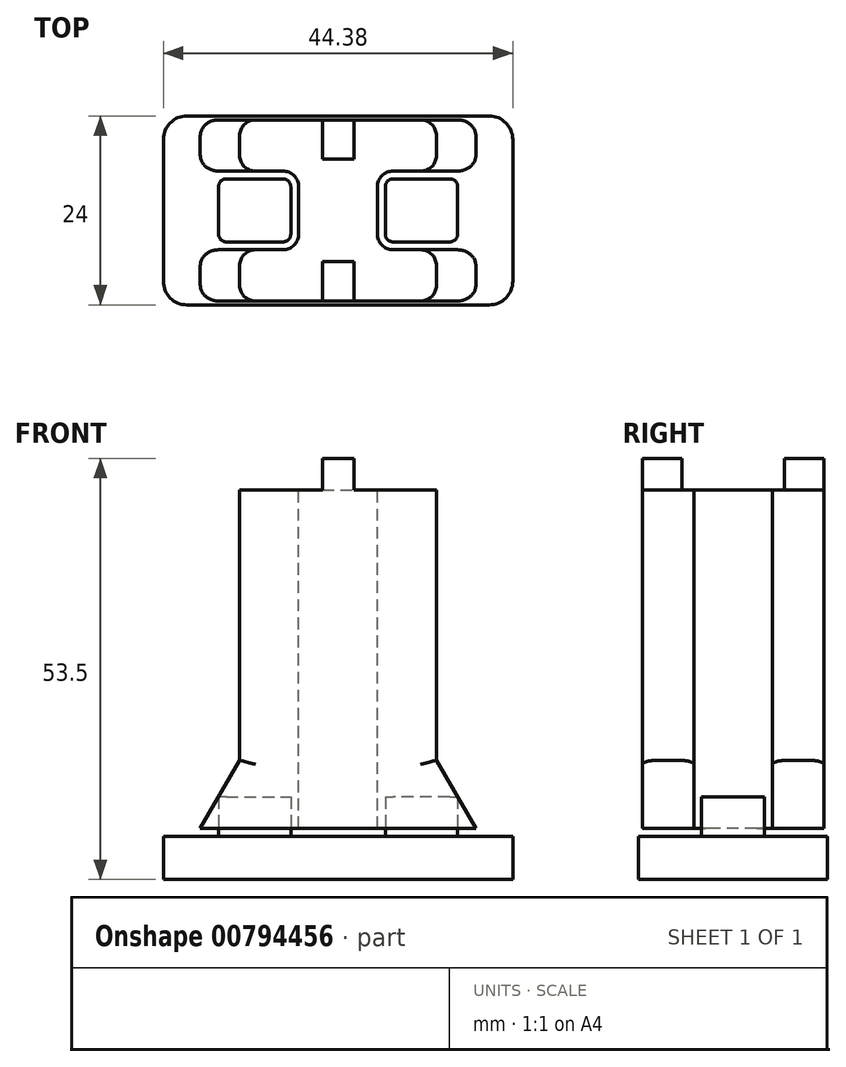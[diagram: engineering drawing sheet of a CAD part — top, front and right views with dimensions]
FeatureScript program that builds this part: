
annotation { "Feature Type Name" : "Feature", "Feature Type Description" : "" }
export const myFeature = defineFeature(function(context is Context, id is Id, definition is map)
    precondition{}
    {
        {
            var Q0;
            Q0=qCreatedBy(makeId("Top.planeOp"),FACE);
            var sketch = newSketch(context, id + "F0", { "sketchPlane" : qUnion([Q0])});
            skLineSegment(sketch, "E0.bottom", {"start": v(0, 0) * mm, "end": v(25, 0) * mm});
            skLineSegment(sketch, "E0.top", {"start": v(0, -23) * mm, "end": v(25, -23) * mm});
            skLineSegment(sketch, "E0.left", {"start": v(0, 0) * mm, "end": v(0, -23) * mm});
            skLineSegment(sketch, "E0.right", {"start": v(25, 0) * mm, "end": v(25, -23) * mm});
            skSolve(sketch);
        }
        {
            var Q0;
            Q0 = qSketchRegion(id + "F0", true);
            extrude(context, id + "F1", {"entities" : qUnion([Q0]), "depth" : 43 * mm, "offsetDistance" : 25 * mm});
        }
        {
            var Q0;
            Q0=makeQuery(id+"F1.opExtrude","CAP_FACE",FACE,{"disambiguationData":[OSD([sQuery(id+"F0.wireOp",EDGE,"E0.bottom"),sQuery(id+"F0.wireOp",EDGE,"E0.top"),sQuery(id+"F0.wireOp",EDGE,"E0.left"),sQuery(id+"F0.wireOp",EDGE,"E0.right")])],"isStart":false});
            var sketch = newSketch(context, id + "F2", { "sketchPlane" : qUnion([Q0])});
            skLineSegment(sketch, "E1.bottom", {"start": v(10.5, 0) * mm, "end": v(14.5, 0) * mm});
            skLineSegment(sketch, "E1.top", {"start": v(10.5, -5) * mm, "end": v(14.5, -5) * mm});
            skLineSegment(sketch, "E1.left", {"start": v(10.5, 0) * mm, "end": v(10.5, -5) * mm});
            skLineSegment(sketch, "E1.right", {"start": v(14.5, 0) * mm, "end": v(14.5, -5) * mm});
            skLineSegment(sketch, "E2.bottom", {"start": v(10.5, -23) * mm, "end": v(14.5, -23) * mm});
            skLineSegment(sketch, "E2.top", {"start": v(10.5, -18) * mm, "end": v(14.5, -18) * mm});
            skLineSegment(sketch, "E2.left", {"start": v(10.5, -23) * mm, "end": v(10.5, -18) * mm});
            skLineSegment(sketch, "E2.right", {"start": v(14.5, -23) * mm, "end": v(14.5, -18) * mm});
            skSolve(sketch);
        }
        {
            var Q0;
            Q0 = qSketchRegion(id + "F2", true);
            extrude(context, id + "F3", {"entities" : qUnion([Q0]), "operationType" : NewBodyOperationType.ADD, "depth" : 4 * mm, "offsetDistance" : 25 * mm});
        }
        {
            var Q0;
            Q0=makeQuery(id+"F3.boolean.opBoolean","MERGE",FACE,{"derivedFrom":[makeQuery(id+"F1.opExtrude","SWEPT_FACE",FACE,{"disambiguationData":[OSD([sQuery(id+"F0.wireOp",EDGE,"E0.top")])]}),makeQuery(id+"F3.opExtrude","SWEPT_FACE",FACE,{"disambiguationData":[OSD([sQuery(id+"F2.wireOp",EDGE,"E2.bottom")])]})]});
            var sketch = newSketch(context, id + "F4", { "sketchPlane" : qUnion([Q0])});
            skLineSegment(sketch, "E3", {"start": v(25, 8.66) * mm, "end": v(30, 0) * mm});
            skLineSegment(sketch, "E4", {"start": v(30, 0) * mm, "end": v(25, 0) * mm});
            skLineSegment(sketch, "E5", {"start": v(25, 0) * mm, "end": v(25, 8.66) * mm});
            skLineSegment(sketch, "E6", {"start": v(0, 8.66) * mm, "end": v(-5, 0) * mm});
            skLineSegment(sketch, "E7", {"start": v(-5, 0) * mm, "end": v(0, 0) * mm});
            skLineSegment(sketch, "E8", {"start": v(0, 0) * mm, "end": v(0, 8.66) * mm});
            skSolve(sketch);
        }
        {
            var Q0;
            Q0 = qSketchRegion(id + "F4", true);
            extrude(context, id + "F5", {"entities" : qUnion([Q0]), "operationType" : NewBodyOperationType.ADD, "oppositeDirection" : true, "depth" : 23 * mm, "offsetDistance" : 25 * mm});
        }
        {
            var Q0;
            Q0=makeQuery(id+"F1.opExtrude","CAP_FACE",FACE,{"disambiguationData":[OSD([sQuery(id+"F0.wireOp",EDGE,"E0.bottom"),sQuery(id+"F0.wireOp",EDGE,"E0.top"),sQuery(id+"F0.wireOp",EDGE,"E0.left"),sQuery(id+"F0.wireOp",EDGE,"E0.right")])],"isStart":false});
            var sketch = newSketch(context, id + "F6", { "sketchPlane" : qUnion([Q0])});
            skLineSegment(sketch, "E9.bottom", {"start": v(-7.5, -6.5) * mm, "end": v(7.5, -6.5) * mm});
            skLineSegment(sketch, "E9.top", {"start": v(-7.5, -16.5) * mm, "end": v(7.5, -16.5) * mm});
            skLineSegment(sketch, "E9.left", {"start": v(-7.5, -6.5) * mm, "end": v(-7.5, -16.5) * mm});
            skLineSegment(sketch, "E9.right", {"start": v(7.5, -6.5) * mm, "end": v(7.5, -16.5) * mm});
            skPoint(sketch, "E9.middle", {"position": v(0, -11.5) * mm});
            skLineSegment(sketch, "E10.bottom", {"start": v(32.5, -6.5) * mm, "end": v(17.5, -6.5) * mm});
            skLineSegment(sketch, "E10.top", {"start": v(32.5, -16.5) * mm, "end": v(17.5, -16.5) * mm});
            skLineSegment(sketch, "E10.left", {"start": v(32.5, -6.5) * mm, "end": v(32.5, -16.5) * mm});
            skLineSegment(sketch, "E10.right", {"start": v(17.5, -6.5) * mm, "end": v(17.5, -16.5) * mm});
            skPoint(sketch, "E10.middle", {"position": v(25, -11.5) * mm});
            skPoint(sketch, "E10.cornerSnap0", {"position": v(0, -6.5) * mm});
            skSolve(sketch);
        }
        {
            var Q0;
            Q0 = qSketchRegion(id + "F6", true);
            extrude(context, id + "F7", {"entities" : qUnion([Q0]), "operationType" : NewBodyOperationType.REMOVE, "endBound" : BoundingType.THROUGH_ALL, "oppositeDirection" : true, "depth" : 25 * mm, "offsetDistance" : 25 * mm});
        }
        {
            var Q0;
            Q0=makeQuery(id+"F1.opExtrude","SWEPT_EDGE",EDGE,{"disambiguationData":[OSD([sQuery(id+"F0.wireOp",EDGE,"E0.top"),sQuery(id+"F0.wireOp",EDGE,"E0.right")])]});
            var Q1;
            Q1=makeQuery(id+"F5.opExtrude","CAP_EDGE",EDGE,{"disambiguationData":[OSD([sQuery(id+"F4.wireOp",EDGE,"E3")])],"isStart":true});
            var Q2;
            Q2=makeQuery(id+"F1.opExtrude","SWEPT_EDGE",EDGE,{"disambiguationData":[OSD([sQuery(id+"F0.wireOp",EDGE,"E0.top"),sQuery(id+"F0.wireOp",EDGE,"E0.left")])]});
            var Q3;
            Q3=makeQuery(id+"F7.boolean.opBoolean","INTERSECT",EDGE,{"derivedFrom":[makeQuery(id+"F1.opExtrude","SWEPT_FACE",FACE,{"disambiguationData":[OSD([sQuery(id+"F0.wireOp",EDGE,"E0.left")])]}),makeQuery(id+"F7.opExtrude","SWEPT_FACE",FACE,{"disambiguationData":[OSD([sQuery(id+"F6.wireOp",EDGE,"E9.top")])]})]});
            var Q4;
            Q4=makeQuery(id+"F5.opExtrude","CAP_EDGE",EDGE,{"disambiguationData":[OSD([sQuery(id+"F4.wireOp",EDGE,"E6")])],"isStart":true});
            var Q5;
            Q5=makeQuery(id+"F7.boolean.opBoolean","INTERSECT",EDGE,{"derivedFrom":[makeQuery(id+"F5.opExtrude","SWEPT_FACE",FACE,{"disambiguationData":[OSD([sQuery(id+"F4.wireOp",EDGE,"E6")])]}),makeQuery(id+"F7.opExtrude","SWEPT_FACE",FACE,{"disambiguationData":[OSD([sQuery(id+"F6.wireOp",EDGE,"E9.top")])]})]});
            var Q6;
            Q6=makeQuery(id+"F7.boolean.opBoolean","COPY",EDGE,{"derivedFrom":makeQuery(id+"F7.opExtrude","SWEPT_EDGE",EDGE,{"disambiguationData":[OSD([sQuery(id+"F6.wireOp",EDGE,"E9.top"),sQuery(id+"F6.wireOp",EDGE,"E9.right")])]})});
            var Q7;
            Q7=makeQuery(id+"F7.boolean.opBoolean","COPY",EDGE,{"derivedFrom":makeQuery(id+"F7.opExtrude","SWEPT_EDGE",EDGE,{"disambiguationData":[OSD([sQuery(id+"F6.wireOp",EDGE,"E9.bottom"),sQuery(id+"F6.wireOp",EDGE,"E9.right")])]})});
            var Q8;
            Q8=makeQuery(id+"F7.boolean.opBoolean","INTERSECT",EDGE,{"derivedFrom":[makeQuery(id+"F1.opExtrude","SWEPT_FACE",FACE,{"disambiguationData":[OSD([sQuery(id+"F0.wireOp",EDGE,"E0.left")])]}),makeQuery(id+"F7.opExtrude","SWEPT_FACE",FACE,{"disambiguationData":[OSD([sQuery(id+"F6.wireOp",EDGE,"E9.bottom")])]})]});
            var Q9;
            Q9=makeQuery(id+"F7.boolean.opBoolean","INTERSECT",EDGE,{"derivedFrom":[makeQuery(id+"F5.opExtrude","SWEPT_FACE",FACE,{"disambiguationData":[OSD([sQuery(id+"F4.wireOp",EDGE,"E6")])]}),makeQuery(id+"F7.opExtrude","SWEPT_FACE",FACE,{"disambiguationData":[OSD([sQuery(id+"F6.wireOp",EDGE,"E9.bottom")])]})]});
            var Q10;
            Q10=makeQuery(id+"F1.opExtrude","SWEPT_EDGE",EDGE,{"disambiguationData":[OSD([sQuery(id+"F0.wireOp",EDGE,"E0.bottom"),sQuery(id+"F0.wireOp",EDGE,"E0.left")])]});
            var Q11;
            Q11=makeQuery(id+"F5.opExtrude","CAP_EDGE",EDGE,{"disambiguationData":[OSD([sQuery(id+"F4.wireOp",EDGE,"E6")])],"isStart":false});
            var Q12;
            Q12=makeQuery(id+"F7.boolean.opBoolean","COPY",EDGE,{"derivedFrom":makeQuery(id+"F7.opExtrude","SWEPT_EDGE",EDGE,{"disambiguationData":[OSD([sQuery(id+"F6.wireOp",EDGE,"E10.top"),sQuery(id+"F6.wireOp",EDGE,"E10.right")])]})});
            var Q13;
            Q13=makeQuery(id+"F7.boolean.opBoolean","INTERSECT",EDGE,{"derivedFrom":[makeQuery(id+"F1.opExtrude","SWEPT_FACE",FACE,{"disambiguationData":[OSD([sQuery(id+"F0.wireOp",EDGE,"E0.right")])]}),makeQuery(id+"F7.opExtrude","SWEPT_FACE",FACE,{"disambiguationData":[OSD([sQuery(id+"F6.wireOp",EDGE,"E10.top")])]})]});
            var Q14;
            Q14=makeQuery(id+"F7.boolean.opBoolean","INTERSECT",EDGE,{"derivedFrom":[makeQuery(id+"F5.opExtrude","SWEPT_FACE",FACE,{"disambiguationData":[OSD([sQuery(id+"F4.wireOp",EDGE,"E3")])]}),makeQuery(id+"F7.opExtrude","SWEPT_FACE",FACE,{"disambiguationData":[OSD([sQuery(id+"F6.wireOp",EDGE,"E10.top")])]})]});
            var Q15;
            Q15=makeQuery(id+"F5.opExtrude","CAP_EDGE",EDGE,{"disambiguationData":[OSD([sQuery(id+"F4.wireOp",EDGE,"E3")])],"isStart":false});
            var Q16;
            Q16=makeQuery(id+"F1.opExtrude","SWEPT_EDGE",EDGE,{"disambiguationData":[OSD([sQuery(id+"F0.wireOp",EDGE,"E0.bottom"),sQuery(id+"F0.wireOp",EDGE,"E0.right")])]});
            var Q17;
            Q17=makeQuery(id+"F7.boolean.opBoolean","COPY",EDGE,{"derivedFrom":makeQuery(id+"F7.opExtrude","SWEPT_EDGE",EDGE,{"disambiguationData":[OSD([sQuery(id+"F6.wireOp",EDGE,"E10.bottom"),sQuery(id+"F6.wireOp",EDGE,"E10.right")])]})});
            var Q18;
            Q18=makeQuery(id+"F7.boolean.opBoolean","INTERSECT",EDGE,{"derivedFrom":[makeQuery(id+"F1.opExtrude","SWEPT_FACE",FACE,{"disambiguationData":[OSD([sQuery(id+"F0.wireOp",EDGE,"E0.right")])]}),makeQuery(id+"F7.opExtrude","SWEPT_FACE",FACE,{"disambiguationData":[OSD([sQuery(id+"F6.wireOp",EDGE,"E10.bottom")])]})]});
            var Q19;
            Q19=makeQuery(id+"F7.boolean.opBoolean","INTERSECT",EDGE,{"derivedFrom":[makeQuery(id+"F5.opExtrude","SWEPT_FACE",FACE,{"disambiguationData":[OSD([sQuery(id+"F4.wireOp",EDGE,"E3")])]}),makeQuery(id+"F7.opExtrude","SWEPT_FACE",FACE,{"disambiguationData":[OSD([sQuery(id+"F6.wireOp",EDGE,"E10.bottom")])]})]});
            fillet(context, id + "F8", {"entities" : qUnion([Q0, Q1, Q2, Q3, Q4, Q5, Q6, Q7, Q8, Q9, Q10, Q11, Q12, Q13, Q14, Q15, Q16, Q17, Q18, Q19]), "radius" : 2 * mm, "tangentPropagation" : true, "allowEdgeOverflow" : false});
        }
        {
            var Q0;
            Q0=makeQuery(id+"F5.boolean.opBoolean","MERGE",FACE,{"derivedFrom":[makeQuery(id+"F1.opExtrude","CAP_FACE",FACE,{"disambiguationData":[OSD([sQuery(id+"F0.wireOp",EDGE,"E0.bottom"),sQuery(id+"F0.wireOp",EDGE,"E0.top"),sQuery(id+"F0.wireOp",EDGE,"E0.left"),sQuery(id+"F0.wireOp",EDGE,"E0.right")])],"isStart":true}),makeQuery(id+"F5.opExtrude","SWEPT_FACE",FACE,{"disambiguationData":[OSD([sQuery(id+"F4.wireOp",EDGE,"E4")])]}),makeQuery(id+"F5.opExtrude","SWEPT_FACE",FACE,{"disambiguationData":[OSD([sQuery(id+"F4.wireOp",EDGE,"E7")])]})]});
            var sketch = newSketch(context, id + "F9", { "sketchPlane" : qUnion([Q0])});
            skLineSegment(sketch, "E11.0", {"start": v(-2.7, 15.5) * mm, "end": v(5.5, 15.5) * mm});
            skLineSegment(sketch, "E12.0", {"start": v(6.5, 8.5) * mm, "end": v(6.5, 14.5) * mm});
            skLineSegment(sketch, "E13.0", {"start": v(-2.7, 7.5) * mm, "end": v(5.5, 7.5) * mm});
            skLineSegment(sketch, "E14.0", {"start": v(18.5, 8.5) * mm, "end": v(18.5, 14.5) * mm});
            skLineSegment(sketch, "E15.0", {"start": v(27.7, 15.5) * mm, "end": v(19.5, 15.5) * mm});
            skLineSegment(sketch, "E16.0", {"start": v(27.7, 7.5) * mm, "end": v(19.5, 7.5) * mm});
            skArc(sketch, "E17", {"start": v(6.5, 14.5) * mm, "mid": v(6.2, 15.2) * mm, "end": v(5.5, 15.5) * mm});
            skArc(sketch, "E18", {"start": v(5.5, 7.5) * mm, "mid": v(6.2, 7.8) * mm, "end": v(6.5, 8.5) * mm});
            skArc(sketch, "E19", {"start": v(19.5, 15.5) * mm, "mid": v(18.8, 15.2) * mm, "end": v(18.5, 14.5) * mm});
            skArc(sketch, "E20", {"start": v(18.5, 8.5) * mm, "mid": v(18.8, 7.8) * mm, "end": v(19.5, 7.5) * mm});
            skLineSegment(sketch, "E21", {"start": v(27.7, 15.5) * mm, "end": v(27.7, 7.5) * mm});
            skLineSegment(sketch, "E22", {"start": v(-2.7, 15.5) * mm, "end": v(-2.7, 7.5) * mm});
            skSolve(sketch);
        }
        {
            var Q0;
            Q0 = qSketchRegion(id + "F9", true);
            extrude(context, id + "F10", {"entities" : qUnion([Q0]), "oppositeDirection" : true, "depth" : 4 * mm, "offsetDistance" : 25 * mm, "hasSecondDirection" : true, "secondDirectionOppositeDirection" : false, "secondDirectionDepth" : 1 * mm});
        }
        {
            var Q0;
            Q0=makeQuery(id+"F10.opExtrude","CAP_FACE",FACE,{"disambiguationData":[OSD([sQuery(id+"F9.wireOp",EDGE,"E11.0"),sQuery(id+"F9.wireOp",EDGE,"E12.0"),sQuery(id+"F9.wireOp",EDGE,"E13.0"),sQuery(id+"F9.wireOp",EDGE,"E17"),sQuery(id+"F9.wireOp",EDGE,"E18"),sQuery(id+"F9.wireOp",EDGE,"E22")])],"isStart":true});
            var sketch = newSketch(context, id + "F11", { "sketchPlane" : qUnion([Q0])});
            skLineSegment(sketch, "E23.bottom", {"start": v(-9.7, -0.5) * mm, "end": v(34.7, -0.5) * mm});
            skLineSegment(sketch, "E23.top", {"start": v(-9.7, 23.5) * mm, "end": v(34.7, 23.5) * mm});
            skLineSegment(sketch, "E23.left", {"start": v(-9.7, -0.5) * mm, "end": v(-9.7, 23.5) * mm});
            skLineSegment(sketch, "E23.right", {"start": v(34.7, -0.5) * mm, "end": v(34.7, 23.5) * mm});
            skSolve(sketch);
        }
        {
            var Q0;
            Q0 = qSketchRegion(id + "F11", true);
            extrude(context, id + "F12", {"entities" : qUnion([Q0]), "operationType" : NewBodyOperationType.ADD, "depth" : 5.5 * mm, "offsetDistance" : 25 * mm});
        }
        {
            var Q0;
            Q0=makeQuery(id+"F12.opExtrude","SWEPT_EDGE",EDGE,{"disambiguationData":[OSD([sQuery(id+"F11.wireOp",EDGE,"E23.top"),sQuery(id+"F11.wireOp",EDGE,"E23.right")])]});
            var Q1;
            Q1=makeQuery(id+"F12.opExtrude","SWEPT_EDGE",EDGE,{"disambiguationData":[OSD([sQuery(id+"F11.wireOp",EDGE,"E23.top"),sQuery(id+"F11.wireOp",EDGE,"E23.left")])]});
            var Q2;
            Q2=makeQuery(id+"F12.opExtrude","SWEPT_EDGE",EDGE,{"disambiguationData":[OSD([sQuery(id+"F11.wireOp",EDGE,"E23.bottom"),sQuery(id+"F11.wireOp",EDGE,"E23.left")])]});
            var Q3;
            Q3=makeQuery(id+"F12.opExtrude","SWEPT_EDGE",EDGE,{"disambiguationData":[OSD([sQuery(id+"F11.wireOp",EDGE,"E23.bottom"),sQuery(id+"F11.wireOp",EDGE,"E23.right")])]});
            fillet(context, id + "F13", {"entities" : qUnion([Q0, Q1, Q2, Q3]), "radius" : 3 * mm, "tangentPropagation" : true, "allowEdgeOverflow" : false});
        }
        {
            var Q0;
            Q0=makeQuery(id+"F10.opExtrude","SWEPT_EDGE",EDGE,{"disambiguationData":[OSD([sQuery(id+"F9.wireOp",EDGE,"E15.0"),sQuery(id+"F9.wireOp",EDGE,"E21")])]});
            var Q1;
            Q1=makeQuery(id+"F10.opExtrude","SWEPT_EDGE",EDGE,{"disambiguationData":[OSD([sQuery(id+"F9.wireOp",EDGE,"E16.0"),sQuery(id+"F9.wireOp",EDGE,"E21")])]});
            var Q2;
            Q2=makeQuery(id+"F10.opExtrude","SWEPT_EDGE",EDGE,{"disambiguationData":[OSD([sQuery(id+"F9.wireOp",EDGE,"E13.0"),sQuery(id+"F9.wireOp",EDGE,"E22")])]});
            var Q3;
            Q3=makeQuery(id+"F10.opExtrude","SWEPT_EDGE",EDGE,{"disambiguationData":[OSD([sQuery(id+"F9.wireOp",EDGE,"E11.0"),sQuery(id+"F9.wireOp",EDGE,"E22")])]});
            fillet(context, id + "F14", {"entities" : qUnion([Q0, Q1, Q2, Q3]), "radius" : 1 * mm, "tangentPropagation" : true, "allowEdgeOverflow" : false});
        }
    });
